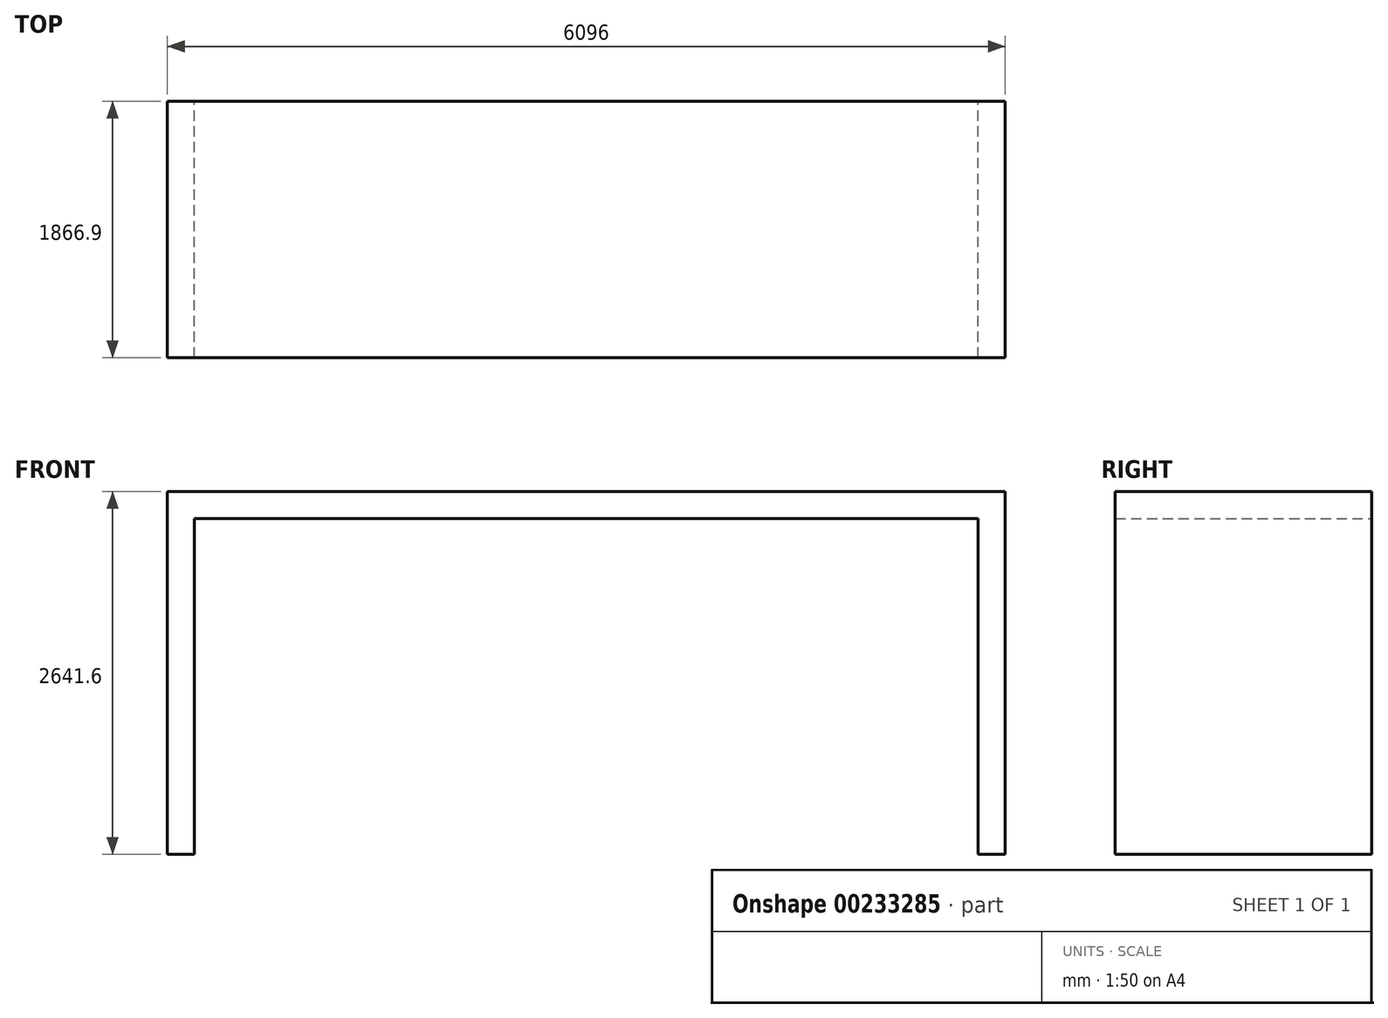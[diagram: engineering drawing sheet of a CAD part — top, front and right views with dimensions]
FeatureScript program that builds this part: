
annotation { "Feature Type Name" : "Feature", "Feature Type Description" : "" }
export const myFeature = defineFeature(function(context is Context, id is Id, definition is map)
    precondition{}
    {
        {
            var Q0;
            Q0=qCreatedBy(makeId("Front.planeOp"),FACE);
            var sketch = newSketch(context, id + "F0", { "sketchPlane" : qUnion([Q0])});
            skLineSegment(sketch, "E0", {"start": v(-3045.17, 1857.8) * mm, "end": v(3050.83, 1857.8) * mm});
            skLineSegment(sketch, "E1", {"start": v(3050.83, 1857.8) * mm, "end": v(3050.83, -783.8) * mm});
            skLineSegment(sketch, "E2", {"start": v(3050.83, -783.8) * mm, "end": v(2853.98, -783.8) * mm});
            skLineSegment(sketch, "E3", {"start": v(2853.98, -783.8) * mm, "end": v(2853.98, 1660.96) * mm});
            skLineSegment(sketch, "E4", {"start": v(2853.98, 1660.96) * mm, "end": v(-2848.32, 1660.96) * mm});
            skLineSegment(sketch, "E5", {"start": v(-2848.32, 1660.96) * mm, "end": v(-2848.32, -783.8) * mm});
            skLineSegment(sketch, "E6", {"start": v(-2848.32, -783.8) * mm, "end": v(-3045.17, -783.8) * mm});
            skLineSegment(sketch, "E7", {"start": v(-3045.17, -783.8) * mm, "end": v(-3045.17, 1857.8) * mm});
            skSolve(sketch);
        }
        {
            var Q0;
            Q0=makeQuery(id+"F0.imprint","IMPRINT",FACE,{"disambiguationData":[TD([[makeQuery(id+"F0.imprint","IMPRINT",EDGE,{"derivedFrom":sQuery(id+"F0.wireOp",EDGE,"E0")}),-1.0]])]});
            extrude(context, id + "F1", {"entities" : qUnion([Q0]), "depth" : 1866.9 * mm});
        }
    });
